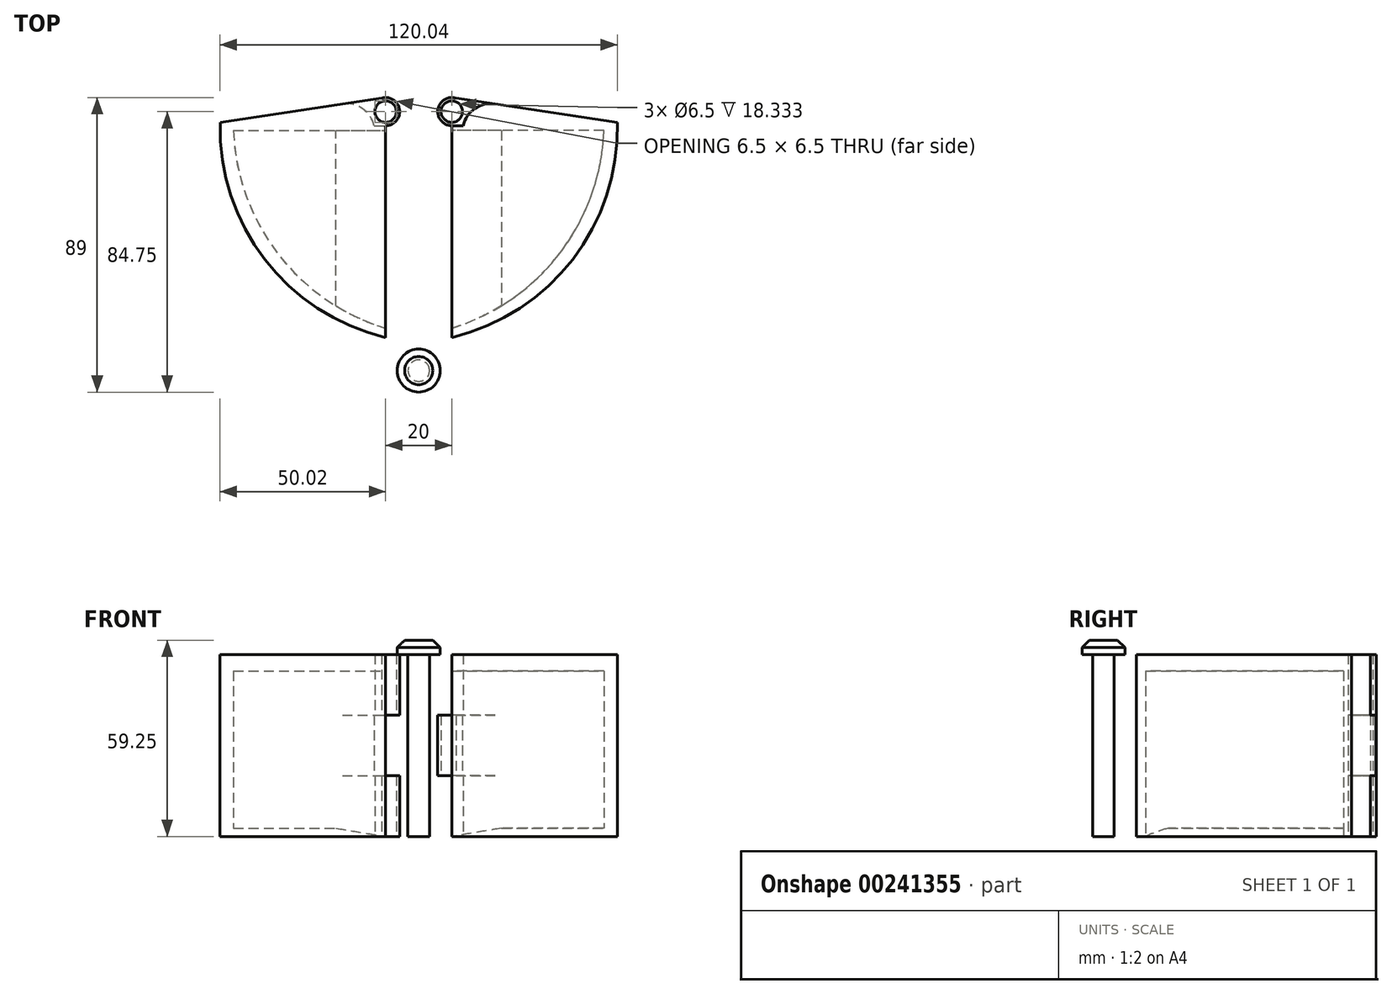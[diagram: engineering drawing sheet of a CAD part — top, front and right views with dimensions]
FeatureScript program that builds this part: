
annotation { "Feature Type Name" : "Feature", "Feature Type Description" : "" }
export const myFeature = defineFeature(function(context is Context, id is Id, definition is map)
    precondition{}
    {
        {
            var Q0;
            Q0=qCreatedBy(makeId("Top.planeOp"),FACE);
            var sketch = newSketch(context, id + "F0", { "sketchPlane" : qUnion([Q0])});
            skLineSegment(sketch, "E0", {"start": v(-10, 10) * mm, "end": v(-10, 75) * mm});
            skLineSegment(sketch, "E1", {"start": v(-10, 75) * mm, "end": v(-60, 75) * mm});
            skArc(sketch, "E2", {"start": v(-60, 75) * mm, "mid": v(-46.54, 33.62) * mm, "end": v(-10, 10) * mm});
            skArc(sketch, "E3.MirrorCS", {"start": v(60, 75) * mm, "mid": v(46.54, 33.62) * mm, "end": v(10, 10) * mm});
            skLineSegment(sketch, "E4.MirrorCS", {"start": v(10, 75) * mm, "end": v(60, 75) * mm});
            skLineSegment(sketch, "E5.MirrorCS", {"start": v(10, 10) * mm, "end": v(10, 75) * mm});
            skSolve(sketch);
        }
        {
            var Q0;
            Q0=qCreatedBy(makeId("Top.planeOp"),FACE);
            var sketch = newSketch(context, id + "F1", { "sketchPlane" : qUnion([Q0])});
            skLineSegment(sketch, "E6", {"start": v(-56, 72.5) * mm, "end": v(-9, 72.5) * mm});
            skLineSegment(sketch, "E7", {"start": v(-9, 72.5) * mm, "end": v(-9, 12.5) * mm});
            skArc(sketch, "E8", {"start": v(-56, 72.5) * mm, "mid": v(-42.22, 34.89) * mm, "end": v(-9, 12.5) * mm});
            skLineSegment(sketch, "E9.MirrorCS", {"start": v(56, 72.5) * mm, "end": v(9, 72.5) * mm});
            skArc(sketch, "E10.MirrorCS", {"start": v(56, 72.5) * mm, "mid": v(42.22, 34.89) * mm, "end": v(9, 12.5) * mm});
            skLineSegment(sketch, "E11.MirrorCS", {"start": v(9, 72.5) * mm, "end": v(9, 12.5) * mm});
            skSolve(sketch);
        }
        {
            var Q0;
            Q0 = qSketchRegion(id + "F0", true);
            extrude(context, id + "F2", {"entities" : qUnion([Q0]), "depth" : 55 * mm});
        }
        {
            var Q0;
            Q0 = qSketchRegion(id + "F1", true);
            extrude(context, id + "F3", {"entities" : qUnion([Q0]), "operationType" : NewBodyOperationType.REMOVE, "depth" : 50 * mm, "hasSecondDirection" : true, "secondDirectionOppositeDirection" : false, "secondDirectionDepth" : 2.5 * mm});
        }
        {
            var Q0;
            Q0=makeQuery(id+"F3.boolean.opBoolean","INTERSECT",EDGE,{"derivedFrom":[makeQuery(id+"F2.opExtrude","SWEPT_FACE",FACE,{"disambiguationData":[OSD([sQuery(id+"F0.wireOp",EDGE,"E5.MirrorCS")])]}),makeQuery(id+"F3.opExtrude","CAP_FACE",FACE,{"disambiguationData":[OSD([sQuery(id+"F1.wireOp",EDGE,"E9.MirrorCS"),sQuery(id+"F1.wireOp",EDGE,"E10.MirrorCS"),sQuery(id+"F1.wireOp",EDGE,"E11.MirrorCS")])],"isStart":true})]});
            chamfer(context, id + "F4", {"entities" : qUnion([Q0]), "chamferType" : ChamferType.TWO_OFFSETS, "width1" : 2.5 * mm, "oppositeDirection" : false, "width2" : 15 * mm, "tangentPropagation" : true});
        }
        {
            var Q0;
            Q0=makeQuery(id+"F3.boolean.opBoolean","INTERSECT",EDGE,{"derivedFrom":[makeQuery(id+"F2.opExtrude","SWEPT_FACE",FACE,{"disambiguationData":[OSD([sQuery(id+"F0.wireOp",EDGE,"E0")])]}),makeQuery(id+"F3.opExtrude","CAP_FACE",FACE,{"disambiguationData":[OSD([sQuery(id+"F1.wireOp",EDGE,"E6"),sQuery(id+"F1.wireOp",EDGE,"E7"),sQuery(id+"F1.wireOp",EDGE,"E8")])],"isStart":true})]});
            chamfer(context, id + "F5", {"entities" : qUnion([Q0]), "chamferType" : ChamferType.TWO_OFFSETS, "width1" : 15 * mm, "oppositeDirection" : false, "width2" : 2.5 * mm, "tangentPropagation" : true});
        }
        {
            var Q0;
            Q0=qCreatedBy(makeId("Top.planeOp"),FACE);
            var sketch = newSketch(context, id + "F6", { "sketchPlane" : qUnion([Q0])});
            skCircle(sketch, "E12", {"center": v(-10, 78.25) * mm, "radius": 4.25 * mm});
            skCircle(sketch, "E13", {"center": v(-10, 78.25) * mm, "radius": 3.25 * mm});
            skCircle(sketch, "E14.MirrorC", {"center": v(10, 78.25) * mm, "radius": 4.25 * mm});
            skCircle(sketch, "E15.MirrorC", {"center": v(10, 78.25) * mm, "radius": 3.25 * mm});
            skLineSegment(sketch, "E16", {"start": v(-10, 82.5) * mm, "end": v(-60, 75) * mm});
            skLineSegment(sketch, "E17", {"start": v(-60, 75) * mm, "end": v(-10, 75) * mm});
            skLineSegment(sketch, "E18", {"start": v(-10, 75) * mm, "end": v(-10, 82.5) * mm});
            skLineSegment(sketch, "E19.MirrorCS", {"start": v(10, 82.5) * mm, "end": v(60, 75) * mm});
            skLineSegment(sketch, "E20.MirrorCS", {"start": v(10, 75) * mm, "end": v(10, 82.5) * mm});
            skLineSegment(sketch, "E21.MirrorCS", {"start": v(60, 75) * mm, "end": v(10, 75) * mm});
            skSolve(sketch);
        }
        {
            var Q0;
            Q0 = qSketchRegion(id + "F6", true);
            var Q1;
            Q1=makeQuery(id+"F2.opExtrude","CAP_FACE",FACE,{"disambiguationData":[OSD([sQuery(id+"F0.wireOp",EDGE,"E0"),sQuery(id+"F0.wireOp",EDGE,"E1"),sQuery(id+"F0.wireOp",EDGE,"E2")])],"isStart":false});
            extrude(context, id + "F7", {"entities" : qUnion([Q0]), "operationType" : NewBodyOperationType.ADD, "endBound" : BoundingType.UP_TO_SURFACE, "endBoundEntityFace" : qUnion([Q1]), "depth" : 25 * mm});
        }
        {
            var Q0;
            Q0=qCreatedBy(makeId("Right.planeOp"),FACE);
            var sketch = newSketch(context, id + "F8", { "sketchPlane" : qUnion([Q0])});
            skLineSegment(sketch, "E22.bottom", {"start": v(74, 55) * mm, "end": v(82.5, 55) * mm});
            skLineSegment(sketch, "E22.top", {"start": v(74, 0) * mm, "end": v(82.5, 0) * mm});
            skLineSegment(sketch, "E22.left", {"start": v(74, 55) * mm, "end": v(74, 0) * mm});
            skLineSegment(sketch, "E22.right", {"start": v(82.5, 55) * mm, "end": v(82.5, 0) * mm});
            skLineSegment(sketch, "E23", {"start": v(74, 36.67) * mm, "end": v(82.5, 36.67) * mm});
            skLineSegment(sketch, "E24", {"start": v(74, 18.33) * mm, "end": v(82.5, 18.33) * mm});
            skSolve(sketch);
        }
        {
            var Q0;
            {var subQ0=sQuery(id+"F8.wireOp",EDGE,"E22.bottom");Q0=makeQuery(id+"F8.imprint","IMPRINT",FACE,{"disambiguationData":[TD([[makeQuery(id+"F8.imprint","IMPRINT",EDGE,{"derivedFrom":subQ0}),-1.0]])]});}
            var Q1;
            {var subQ0=sQuery(id+"F8.wireOp",EDGE,"E22.top");Q1=makeQuery(id+"F8.imprint","IMPRINT",FACE,{"disambiguationData":[TD([[makeQuery(id+"F8.imprint","IMPRINT",EDGE,{"derivedFrom":subQ0}),1.0]])]});}
            extrude(context, id + "F9", {"entities" : qUnion([Q0, Q1]), "operationType" : NewBodyOperationType.REMOVE, "depth" : 13.5 * mm});
        }
        {
            var Q0;
            {var subQ0=sQuery(id+"F8.wireOp",EDGE,"E23");Q0=makeQuery(id+"F8.imprint","IMPRINT",FACE,{"disambiguationData":[TD([[makeQuery(id+"F8.imprint","IMPRINT",EDGE,{"derivedFrom":subQ0}),-1.0]])]});}
            extrude(context, id + "F10", {"entities" : qUnion([Q0]), "operationType" : NewBodyOperationType.REMOVE, "oppositeDirection" : true, "depth" : 13.5 * mm});
        }
        {
            var Q0;
            Q0=qCreatedBy(makeId("Front.planeOp"),FACE);
            var sketch = newSketch(context, id + "F11", { "sketchPlane" : qUnion([Q0])});
            skLineSegment(sketch, "E25", {"start": v(0, 0) * mm, "end": v(0, 59.25) * mm});
            skLineSegment(sketch, "E26", {"start": v(0, 59.25) * mm, "end": v(-4.25, 59.25) * mm});
            skLineSegment(sketch, "E27", {"start": v(-4.25, 59.25) * mm, "end": v(-6.5, 57.12) * mm});
            skLineSegment(sketch, "E28", {"start": v(-6.5, 57.13) * mm, "end": v(-6.5, 55) * mm});
            skLineSegment(sketch, "E29", {"start": v(-6.5, 55) * mm, "end": v(-3.25, 55) * mm});
            skLineSegment(sketch, "E30", {"start": v(-3.25, 55) * mm, "end": v(-3.25, 0) * mm});
            skLineSegment(sketch, "E31", {"start": v(-3.25, 0) * mm, "end": v(0, 0) * mm});
            skSolve(sketch);
        }
        {
            var Q0;
            Q0=makeQuery(id+"F11.imprint","IMPRINT",FACE,{"disambiguationData":[TD([[makeQuery(id+"F11.imprint","IMPRINT",EDGE,{"derivedFrom":sQuery(id+"F11.wireOp",EDGE,"E25")}),1.0]])]});
            var Q1;
            Q1=sQuery(id+"F11.wireOp",EDGE,"E25");
            revolve(context, id + "F12", {"entities" : qUnion([Q0]), "axis" : qUnion([Q1]), "revolveType" : RevolveType.FULL});
        }
        {
            var Q0;
            Q0=makeQuery(id+"F9.boolean.opBoolean","INTERSECT",EDGE,{"derivedFrom":[makeQuery(id+"F7.opExtrude","SWEPT_FACE",FACE,{"disambiguationData":[OSD([sQuery(id+"F6.wireOp",EDGE,"E19.MirrorCS")])]}),makeQuery(id+"F9.opExtrude","CAP_FACE",FACE,{"disambiguationData":[OSD([sQuery(id+"F8.wireOp",EDGE,"E22.bottom"),sQuery(id+"F8.wireOp",EDGE,"E22.left"),sQuery(id+"F8.wireOp",EDGE,"E22.right"),sQuery(id+"F8.wireOp",EDGE,"E23")])],"isStart":false})]});
            var Q1;
            Q1=makeQuery(id+"F9.boolean.opBoolean","INTERSECT",EDGE,{"derivedFrom":[makeQuery(id+"F7.opExtrude","SWEPT_FACE",FACE,{"disambiguationData":[OSD([sQuery(id+"F6.wireOp",EDGE,"E19.MirrorCS")])]}),makeQuery(id+"F9.opExtrude","CAP_FACE",FACE,{"disambiguationData":[OSD([sQuery(id+"F8.wireOp",EDGE,"E22.top"),sQuery(id+"F8.wireOp",EDGE,"E22.left"),sQuery(id+"F8.wireOp",EDGE,"E22.right"),sQuery(id+"F8.wireOp",EDGE,"E24")])],"isStart":false})]});
            fillet(context, id + "F13", {"entities" : qUnion([Q0, Q1]), "radius" : 8.5 * mm, "tangentPropagation" : true, "allowEdgeOverflow" : false});
        }
        {
            var Q0;
            Q0=makeQuery(id+"F10.boolean.opBoolean","INTERSECT",EDGE,{"derivedFrom":[makeQuery(id+"F7.opExtrude","SWEPT_FACE",FACE,{"disambiguationData":[OSD([sQuery(id+"F6.wireOp",EDGE,"E16")])]}),makeQuery(id+"F10.opExtrude","CAP_FACE",FACE,{"disambiguationData":[OSD([sQuery(id+"F8.wireOp",EDGE,"E22.left"),sQuery(id+"F8.wireOp",EDGE,"E22.right"),sQuery(id+"F8.wireOp",EDGE,"E23"),sQuery(id+"F8.wireOp",EDGE,"E24")])],"isStart":false})]});
            fillet(context, id + "F14", {"entities" : qUnion([Q0]), "radius" : 8.5 * mm, "tangentPropagation" : true, "allowEdgeOverflow" : false});
        }
    });
